# Revit family: PLM-DRN-AEC-Floor
name_source: partatom
category: Plumbing Fixtures
revit_build: Autodesk Revit 2016 (Build: 20150220_1215(x64)
units: mm (PartAtom-declared; Revit-internal decimal feet)

## family parameters
Cut with Voids When Loaded = No
Host = Face
OmniClass Number = 23.45.55.21
OmniClass Title = Drains (Wastes)
Part Type = Normal
Room Calculation Point = No
Round Connector Dimension = Use Diameter
Shared = No

## types (9) — shared parameters
Body Diameter = 206 mm  [stored 0.675853 ft]
Body Radius = 103 mm  [stored 0.337927 ft]
Radius 3 = 52 mm
zero-valued in all types: CWFU, Default Elevation, HWFU

## per-type parameters (varying)
| type | Body Height | Height 1 | Height 2 | Material | Nominal Diameter | Nominal Radius | Radius 1 | Radius 2 | Strainer Half Length | Strainer Height | Strainer Length | WFU |
| 125 mmx125 mm Strainer - 50 mm Drain | 92 mm | 46 mm | 18 mm | <By Category> | 50 mm | 25 mm | 51 mm  [stored 0.167323 ft] | 77 mm  [stored 0.252625 ft] | 63 mm | 83 mm  [stored 0.27231 ft] | 125 mm | 2 |
| 125 mmx125 mm Strainer - 80 mm Drain | 92 mm | 46 mm | 18 mm | <By Category> | 80 mm | 40 mm | 61 mm | 82 mm  [stored 0.269029 ft] | 63 mm | 83 mm  [stored 0.27231 ft] | 125 mm | 3 |
| 125 mmx125 mm Strainer - 100 mm Drain | 92 mm | 46 mm | 18 mm | <By Category> | 100 mm | 50 mm | 68 mm | 85 mm | 63 mm | 83 mm  [stored 0.27231 ft] | 125 mm | 4 |
| 150 mmx150 mm Strainer - 50 mm Drain | 82 mm  [stored 0.269029 ft] | 41 mm  [stored 0.134514 ft] | 16 mm | Steel AISI 1118 | 50 mm | 25 mm | 51 mm  [stored 0.167323 ft] | 77 mm  [stored 0.252625 ft] | 75 mm | 83 mm  [stored 0.27231 ft] | 150 mm | 2 |
| 200 mmx200 mm Strainer - 50 mm Drain | 92 mm | 46 mm | 18 mm | <By Category> | 50 mm | 25 mm | 51 mm  [stored 0.167323 ft] | 77 mm  [stored 0.252625 ft] | 100 mm  [stored 0.328084 ft] | 92 mm | 200 mm | 2 |
| 150 mmx150 mm Strainer - 80 mm Drain | 92 mm | 46 mm | 18 mm | <By Category> | 80 mm | 40 mm | 61 mm | 82 mm  [stored 0.269029 ft] | 75 mm | 83 mm  [stored 0.27231 ft] | 150 mm | 3 |
| 200 mmx200 mm Strainer - 80 mm Drain | 92 mm | 46 mm | 18 mm | <By Category> | 80 mm | 40 mm | 61 mm | 82 mm  [stored 0.269029 ft] | 100 mm  [stored 0.328084 ft] | 83 mm  [stored 0.27231 ft] | 200 mm | 3 |
| 150 mmx150 mm Strainer - 100 mm Drain | 92 mm | 46 mm | 18 mm | <By Category> | 100 mm | 50 mm | 68 mm | 85 mm | 60 mm | 83 mm  [stored 0.27231 ft] | 120 mm | 4 |
| 200 mmx200 mm Strainer - 100 mm Drain | 92 mm | 46 mm | 18 mm | <By Category> | 100 mm | 50 mm | 68 mm | 85 mm | 100 mm  [stored 0.328084 ft] | 92 mm | 200 mm | 4 |

note: [stored X ft] marks values corroborated as IEEE doubles in the binary element streams (Revit-internal decimal feet)

## geometry (parser evidence)
native form markers: Blend x2, Sweep x4
no freeform markers — native parametric forms only
